# Revit family: 0053881 Sylvania Lighting Fixture START eco Downlight Flat Sq 1400lm 840
name_source: partatom
category: Lighting Fixtures
revit_build: Autodesk Revit 2016 (Build: 20150220_1215(x64)
units: mm (PartAtom-declared; Revit-internal decimal feet)

## family parameters
Cut with Voids When Loaded = No
Host = Face
Light Source = Yes
OmniClass Number = 23.80.70.11.14.11
OmniClass Title = Downlights
Part Type = Normal
Room Calculation Point = No
Round Connector Dimension = Use Diameter
Shared = No

## types (1)
- 0053881 START eco Downlight Flat Sq 1400lm 840
    AccessoryMaterial = Diffuser-Sylvania-Glow
    Apparent Load = 0 VA
    Assembly Code = D5020200
    AssetType = Fixed
    BodyLength_FEILO = 220 mm  [stored 0.721785 ft]
    BodyMaterial = Body-Sylvania-SylFlatDimmable-White
    BodyWidth_FEILO = 220 mm  [stored 0.721785 ft]
    ClassificationName = Uniclass2015
    ClassificationValue = EF_70_80
    Color Filter = 16777215
    Cost = 0 $
    CutoutHeight_FEILO = 37 mm
    Default Elevation = 1219 mm
    Description = Integrated square recessed 225mm x 225mm LED downlight providing uniform distribution with an opal diffuser, 110° beam angle, 1440LM, 17W, 85lm/W, 4000K, CRI80, non-dimmable, IP20, IK06, 25,000hrs (L70)
    DiffuserMaterial = Diffuser-Sylvania-Glow
    Dimming Lamp Color Temperature Shift = <None>
    DimmingControlOptions = Non dimmable
    DocumentationLiterature = http://www.feilosylvania.com
    DurationUnit = hours
    ElectricShockClassification = Class II
    Emit Shape Visible in Rendering = No
    Emit from Rectangle Length = 172 mm  [stored 0.564304 ft]
    Emit from Rectangle Width = 172 mm  [stored 0.564304 ft]
    ExpectedLife = 50000
    IfcExportAs = IfcLightFixtureType
    IfcExportType = IfcLightFixtureType
    ImpactProtectionIndex = IK06
    IngressProtection = IP20
    InputNominalFrequency = 50/60 Hz
    InputVoltage = 220-240V~
    Keynote = 16500
    Lamp = LED
    LampColourRenderingIndex = 80
    LampColourTemperature = 3000 K
    LampMacAdamStep = 5
    LampNominalLuminous = 1440 lm
    LampsType = LED
    LightOutputRatio = 1
    LuminaireType = LED recessed downlight
    LuminousEfficacy = 85 lm/W
    Manufacturer = Feilo Sylvania
    ManufacturerName = Feilo Sylvania
    Material = Polycarbonate
    Model = START eco Downlight Flat Sq 1400lm 840
    ModelNumber = 0053881
    ModelReference = START eco Downlight Flat Sq 1400lm 840
    Name = START eco Downlight Flat Sq 1400lm 840
    NominalDepth = 225 mm  [stored 0.738189 ft]
    NominalHeight = 27 mm  [stored 0.0885827 ft]
    NominalLength = 225 mm  [stored 0.738189 ft]
    Photometric Web File = 0053296.ies
    PowerConsumption = 17 W
    PowerFactor = 0
    RadiusDiffuserII_FEILO = 5 mm  [stored 0.0164042 ft]
    RadiusDiffuserI_FEILO = 7 mm  [stored 0.0229659 ft]
    RadiusRecessedII_FEILO = 10 mm  [stored 0.0328084 ft]
    RadiusRecessedI_FEILO = 4 mm  [stored 0.0131234 ft]
    RadiusRimII_FEILO = 17 mm  [stored 0.0557743 ft]
    RadiusRimI_FEILO = 15 mm  [stored 0.0492126 ft]
    RecessedDiameter_FEILO = 205 mm  [stored 0.672572 ft]
    RecessedHeight_FEILO = 27 mm  [stored 0.0885827 ft]
    ReflectorMaterial = <By Category>
    Tilt Angle = -90.00°
    Type Image = <None>
    TypeName = START eco Downlight Flat Sq 1400lm 840
    URL = http://www.feilosylvania.com
    Voltage = 230 V
    WarrantyDurationUnit = year
    Weight = 6.864 kg

note: [stored X ft] marks values corroborated as IEEE doubles in the binary element streams (Revit-internal decimal feet)

## geometry (parser evidence)
native form markers: Sweep x2
no freeform markers — native parametric forms only
